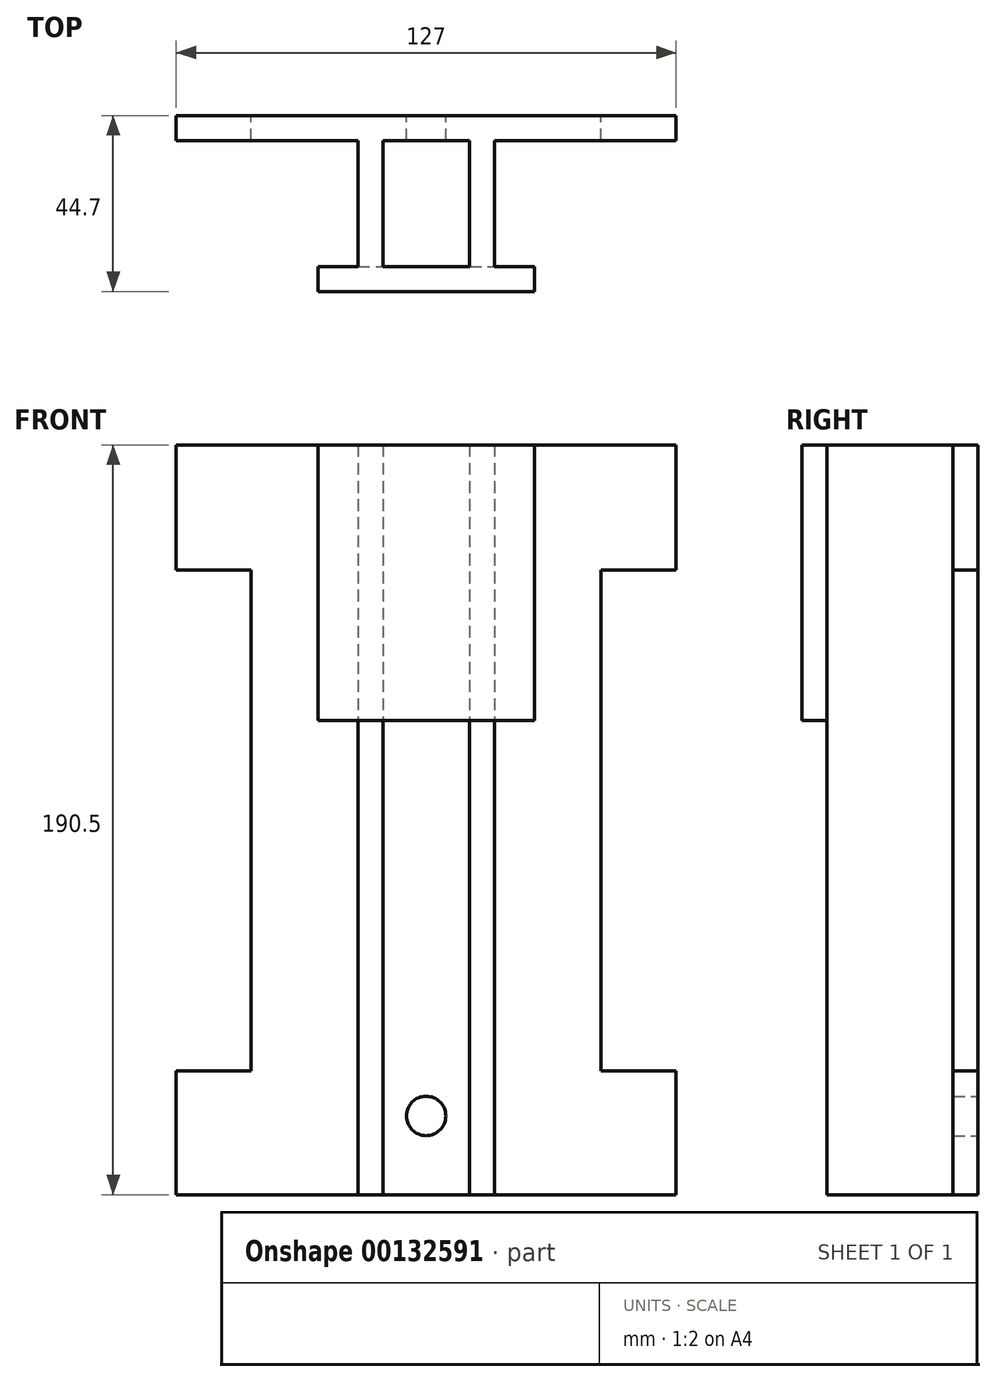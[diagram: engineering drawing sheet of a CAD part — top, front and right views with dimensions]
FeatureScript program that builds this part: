
annotation { "Feature Type Name" : "Feature", "Feature Type Description" : "" }
export const myFeature = defineFeature(function(context is Context, id is Id, definition is map)
    precondition{}
    {
        {
            var Q0;
            Q0=qCreatedBy(makeId("Front.planeOp"),FACE);
            var sketch = newSketch(context, id + "F0", { "sketchPlane" : qUnion([Q0])});
            skLineSegment(sketch, "E0.bottom", {"start": v(0, 0) * mm, "end": v(127, 0) * mm});
            skLineSegment(sketch, "E0.top", {"start": v(0, 190.5) * mm, "end": v(127, 190.5) * mm});
            skLineSegment(sketch, "E0.left", {"start": v(0, 25.1) * mm, "end": v(0, 31.45) * mm});
            skLineSegment(sketch, "E0.right", {"start": v(127, 0) * mm, "end": v(127, 31.45) * mm});
            skPoint(sketch, "E1", {"position": v(127, 165.1) * mm});
            skPoint(sketch, "E2", {"position": v(127, 158.75) * mm});
            skPoint(sketch, "E3", {"position": v(127, 31.45) * mm});
            skPoint(sketch, "E4", {"position": v(127, 25.1) * mm});
            skLineSegment(sketch, "E5.bottom", {"start": v(127, 158.75) * mm, "end": v(107.95, 158.75) * mm});
            skLineSegment(sketch, "E5.top", {"start": v(127, 31.45) * mm, "end": v(107.95, 31.45) * mm});
            skLineSegment(sketch, "E5.right", {"start": v(107.95, 158.75) * mm, "end": v(107.95, 31.45) * mm});
            skLineSegment(sketch, "E6.trimOffspring", {"start": v(127, 158.75) * mm, "end": v(127, 190.5) * mm});
            skPoint(sketch, "E7", {"position": v(63.5, 190.5) * mm});
            skLineSegment(sketch, "E8", {"start": v(63.5, 190.5) * mm, "end": v(63.5, 0) * mm, "construction": true});
            skLineSegment(sketch, "E9.MirrorCS", {"start": v(127, 190.5) * mm, "end": v(0, 190.5) * mm});
            skLineSegment(sketch, "E10.MirrorCS", {"start": v(0, 158.75) * mm, "end": v(0, 190.5) * mm});
            skPoint(sketch, "E11.MirrorP", {"position": v(0, 165.1) * mm});
            skLineSegment(sketch, "E12.MirrorCS", {"start": v(0, 158.75) * mm, "end": v(19.05, 158.75) * mm});
            skLineSegment(sketch, "E13.MirrorCS", {"start": v(19.05, 158.75) * mm, "end": v(19.05, 31.45) * mm});
            skLineSegment(sketch, "E14.MirrorCS", {"start": v(0, 31.45) * mm, "end": v(19.05, 31.45) * mm});
            skPoint(sketch, "E15.MirrorP", {"position": v(0, 31.45) * mm});
            skPoint(sketch, "E16.MirrorP", {"position": v(0, 25.1) * mm});
            skLineSegment(sketch, "E17.MirrorCS", {"start": v(0, 0) * mm, "end": v(0, 31.45) * mm});
            skPoint(sketch, "E18", {"position": v(63.5, 20) * mm});
            skCircle(sketch, "E19", {"center": v(63.5, 20) * mm, "radius": 5 * mm});
            skPoint(sketch, "E20", {"position": v(52.5, 190.5) * mm});
            skLineSegment(sketch, "E21", {"start": v(52.5, 190.5) * mm, "end": v(52.5, 0) * mm});
            skLineSegment(sketch, "E22", {"start": v(46.15, 190.5) * mm, "end": v(46.15, 0) * mm});
            skLineSegment(sketch, "E23.MirrorCS", {"start": v(74.5, 190.5) * mm, "end": v(74.5, 0) * mm});
            skLineSegment(sketch, "E24.MirrorCS", {"start": v(80.85, 190.5) * mm, "end": v(80.85, 0) * mm});
            skSolve(sketch);
        }
        {
            var Q0;
            {var subQ0=sQuery(id+"F0.wireOp",EDGE,"E21");Q0=makeQuery(id+"F0.imprint","IMPRINT",FACE,{"disambiguationData":[TD([[makeQuery(id+"F0.imprint","IMPRINT",EDGE,{"derivedFrom":subQ0}),-1.0]])]});}
            var Q1;
            {var subQ0=sQuery(id+"F0.wireOp",EDGE,"E23.MirrorCS");Q1=makeQuery(id+"F0.imprint","IMPRINT",FACE,{"disambiguationData":[TD([[makeQuery(id+"F0.imprint","IMPRINT",EDGE,{"derivedFrom":subQ0}),1.0]])]});}
            extrude(context, id + "F1", {"entities" : qUnion([Q0, Q1]), "depth" : 32 * mm + 6.35 * mm});
        }
        {
            var Q0;
            Q0 = qSketchRegion(id + "F0", true);
            extrude(context, id + "F2", {"entities" : qUnion([Q0]), "operationType" : NewBodyOperationType.ADD, "depth" : 6.35 * mm});
        }
        {
            var Q0;
            Q0=makeQuery(id+"F1.opExtrude","CAP_FACE",FACE,{"disambiguationData":[OSD([sQuery(id+"F0.wireOp",EDGE,"E0.bottom"),sQuery(id+"F0.wireOp",EDGE,"E0.top"),sQuery(id+"F0.wireOp",EDGE,"E21"),sQuery(id+"F0.wireOp",EDGE,"E22")])],"isStart":false});
            var sketch = newSketch(context, id + "F3", { "sketchPlane" : qUnion([Q0])});
            skLineSegment(sketch, "E25", {"start": v(36, 190.5) * mm, "end": v(36, 120.5) * mm});
            skLineSegment(sketch, "E26", {"start": v(36, 120.5) * mm, "end": v(91, 120.5) * mm});
            skLineSegment(sketch, "E27", {"start": v(36, 190.5) * mm, "end": v(91, 190.5) * mm});
            skLineSegment(sketch, "E28", {"start": v(52.5, 163.58) * mm, "end": v(74.5, 163.58) * mm, "construction": true});
            skPoint(sketch, "E29", {"position": v(63.5, 163.58) * mm});
            skPoint(sketch, "E30", {"position": v(63.5, 120.5) * mm});
            skLineSegment(sketch, "E31", {"start": v(63.5, 163.58) * mm, "end": v(63.5, 120.5) * mm, "construction": true});
            skLineSegment(sketch, "E32", {"start": v(91, 190.5) * mm, "end": v(91, 120.5) * mm});
            skSolve(sketch);
        }
        {
            var Q0;
            Q0 = qSketchRegion(id + "F3", true);
            extrude(context, id + "F4", {"entities" : qUnion([Q0]), "operationType" : NewBodyOperationType.ADD, "depth" : 6.35 * mm});
        }
    });
